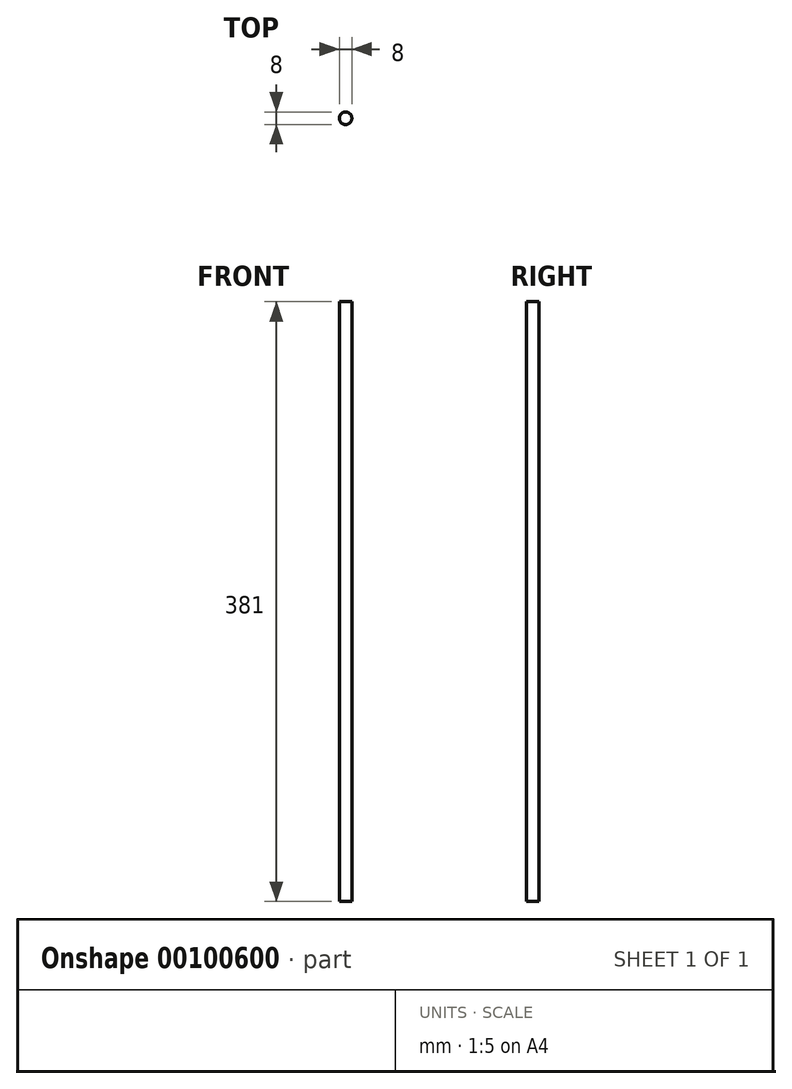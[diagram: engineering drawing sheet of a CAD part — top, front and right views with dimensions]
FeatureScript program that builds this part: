
annotation { "Feature Type Name" : "Feature", "Feature Type Description" : "" }
export const myFeature = defineFeature(function(context is Context, id is Id, definition is map)
    precondition{}
    {
        {
            var Q0;
            Q0=qCreatedBy(makeId("Top.planeOp"),FACE);
            var sketch = newSketch(context, id + "F0", { "sketchPlane" : qUnion([Q0])});
            skCircle(sketch, "E0", {"center": v(0, 0) * mm, "radius": 4 * mm});
            skSolve(sketch);
        }
        {
            var Q0;
            Q0=makeQuery(id+"F0.imprint","IMPRINT",FACE,{"disambiguationData":[TD([[makeQuery(id+"F0.imprint","IMPRINT",EDGE,{"derivedFrom":sQuery(id+"F0.wireOp",EDGE,"E0")}),1.0]])]});
            extrude(context, id + "F1", {"entities" : qUnion([Q0]), "depth" : 381 * mm});
        }
    });
